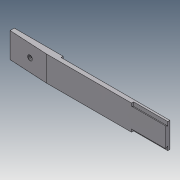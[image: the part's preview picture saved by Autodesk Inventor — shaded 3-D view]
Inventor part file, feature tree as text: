
AUTODESK INVENTOR PART (.ipt)
format: ipt  version: 2018.3 (Build 223284000, 284)  size: 160,256 bytes
history: native  units: in
note: dims shown in document units (in); Inventor stores cm internally (conversion verified against a paired STEP export)
features: sketch x5, extrude x4, projected_geometry x2, mirror x1, hole x1, chamfer x1, fillet x1
ambient origin geometry x8: Origin, YZ Plane, XZ Plane, XY Plane, X Axis, Y Axis, Z Axis, Center Point
bodies: Solid1 (feature_tree)
feature tree (15):
  extrude  "Extrusion1"  Depth=0.24in
  extrude  "Extrusion2"  Depth=0.02in
  mirror  "Mirror1"
  extrude  "Extrusion4"  TaperAngle=60.0deg  [1 undecoded]
  extrude  "Extrusion5"  Depth=0.325in
  hole  "Hole1"  [1 undecoded]
  chamfer  "Chamfer1"  Distance=0.02in
  fillet  "Fillet2"  [1 undecoded]
  sketch  "Sketch1"  dims[d0=1.5in d1=0.24in]
  sketch  "Sketch2"  dims[d2=0.04in d3=0.0in d4=0.02in]
  sketch  "Sketch4"  dims[d5=0.0373in d6=60.0deg]
  projected_geometry  "Projected Loop1"
  sketch  "Sketch5"  dims[d7=0.325in d8=0.0in d15=0.0258in]
  sketch  "Sketch6"  dims[d16=0.0827in d17=0.465in d18=0.02in d19=0.0in d20=60.0deg d21=60.0deg d22=0.083in d23=0.166in d24=0.022in d25=0.38in d26=0.0in d27=0.2in d28=0.047in d29=0.12in d30=0.375in d31=0.25in d32=0.5635in d33=0.183in d34=0.8108in d35=0.365in d36=0.02in d37=45.0deg d38=0.04in]
  projected_geometry  "Projected Loop2"
note: 3 required parameter values undecoded (feature->parameter linkage not recoverable at this tier; creation-order binding heuristic only, values carry confidence <= 0.55)
